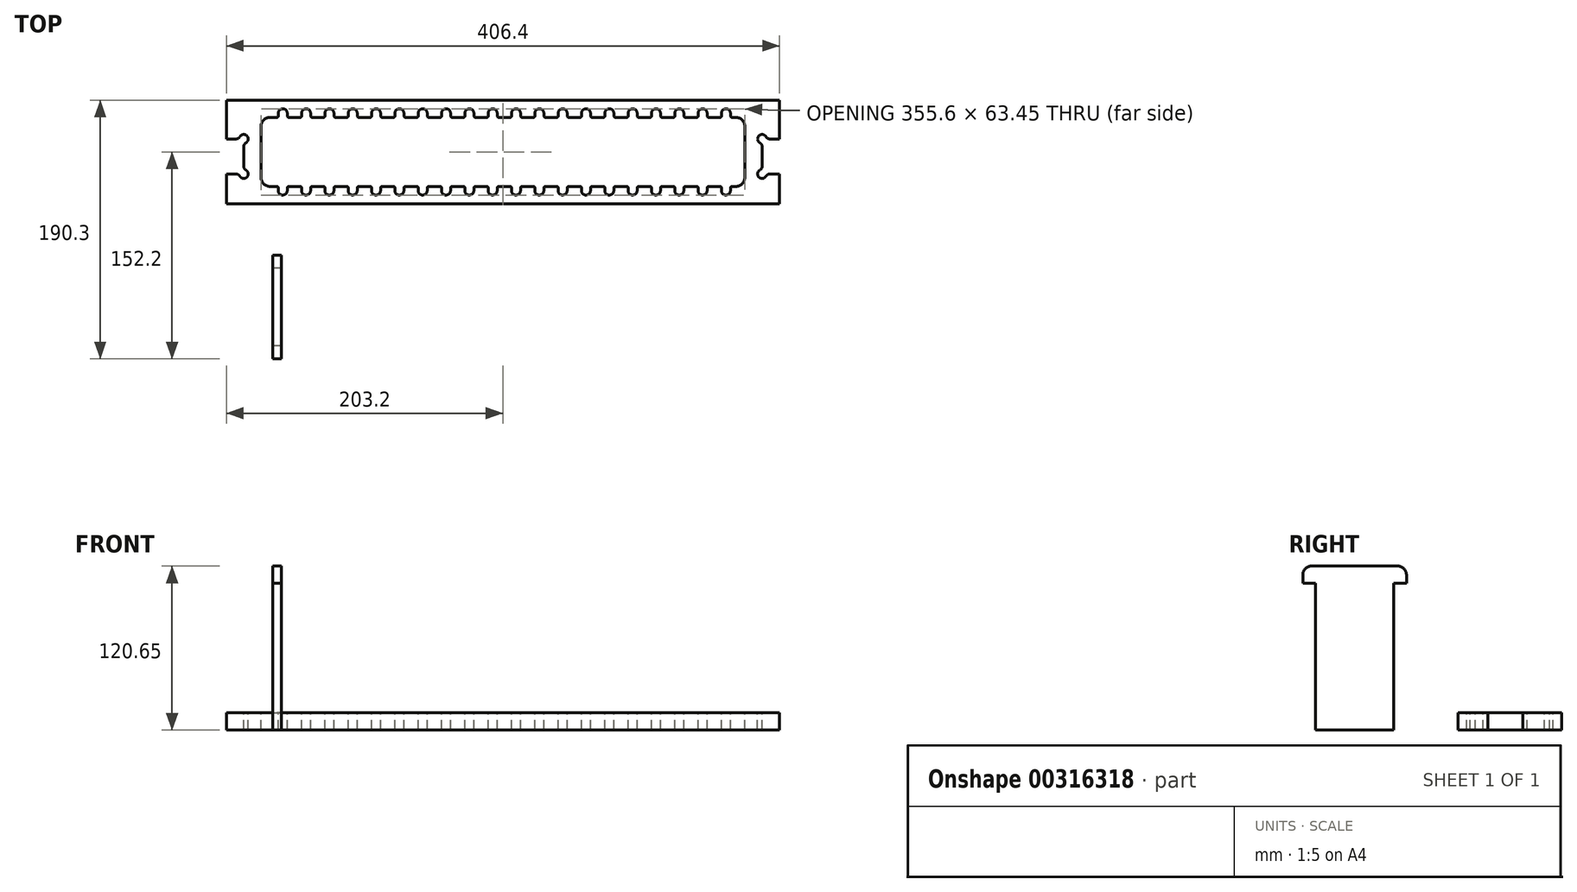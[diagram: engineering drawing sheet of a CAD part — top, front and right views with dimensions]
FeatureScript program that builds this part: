
annotation { "Feature Type Name" : "Feature", "Feature Type Description" : "" }
export const myFeature = defineFeature(function(context is Context, id is Id, definition is map)
    precondition{}
    {
        {
            var Q0;
            Q0=qCreatedBy(makeId("Top.planeOp"),FACE);
            var sketch = newSketch(context, id + "F0", { "sketchPlane" : qUnion([Q0])});
            skLineSegment(sketch, "E0.bottom", {"start": v(0, 0) * mm, "end": v(406.4, 0) * mm});
            skLineSegment(sketch, "E0.top", {"start": v(0, 76.2) * mm, "end": v(406.4, 76.2) * mm});
            skLineSegment(sketch, "E0.left", {"start": v(0, 0) * mm, "end": v(0, 76.2) * mm});
            skLineSegment(sketch, "E0.right", {"start": v(406.4, 0) * mm, "end": v(406.4, 76.2) * mm});
            skSolve(sketch);
        }
        {
            var Q0;
            Q0=qSketchRegion(id+"F0",true);
            extrude(context, id + "F1", {"entities" : qUnion([Q0]), "depth" : 12.7 * mm});
        }
        {
            var Q0;
            Q0=makeQuery(id+"F1.opExtrude","CAP_FACE",FACE,{"disambiguationData":[OSD([sQuery(id+"F0.wireOp",EDGE,"E0.bottom"),sQuery(id+"F0.wireOp",EDGE,"E0.top"),sQuery(id+"F0.wireOp",EDGE,"E0.left"),sQuery(id+"F0.wireOp",EDGE,"E0.right")])],"isStart":false});
            var sketch = newSketch(context, id + "F2", { "sketchPlane" : qUnion([Q0])});
            skLineSegment(sketch, "E1", {"start": v(0, 38.1) * mm, "end": v(103.18, 38.1) * mm, "construction": true});
            skLineSegment(sketch, "E2", {"start": v(203.2, 76.2) * mm, "end": v(203.2, 0) * mm, "construction": true});
            skLineSegment(sketch, "E3.bottom", {"start": v(0, 47.63) * mm, "end": v(7.05, 47.63) * mm});
            skLineSegment(sketch, "E3.top", {"start": v(0, 21.84) * mm, "end": v(7.05, 21.84) * mm});
            skLineSegment(sketch, "E3.left", {"start": v(0, 47.63) * mm, "end": v(0, 21.84) * mm});
            skLineSegment(sketch, "E3.right", {"start": v(12.7, 41.98) * mm, "end": v(12.7, 27.49) * mm});
            skArc(sketch, "E4", {"start": v(14.32, 44.75) * mm, "mid": v(15.03, 49.96) * mm, "end": v(9.82, 49.24) * mm});
            skArc(sketch, "E5", {"start": v(9.82, 20.23) * mm, "mid": v(15.03, 19.5) * mm, "end": v(14.32, 24.72) * mm});
            skPoint(sketch, "E6.visualSharp", {"position": v(9.4, 47.63) * mm});
            skArc(sketch, "E6.filletArc", {"start": v(7.05, 47.63) * mm, "mid": v(8.66, 48.06) * mm, "end": v(9.82, 49.24) * mm});
            skPoint(sketch, "E7.visualSharp", {"position": v(9.4, 21.84) * mm});
            skArc(sketch, "E7.filletArc", {"start": v(9.82, 20.23) * mm, "mid": v(8.66, 21.4) * mm, "end": v(7.05, 21.84) * mm});
            skPoint(sketch, "E8.visualSharp", {"position": v(12.7, 44.32) * mm});
            skArc(sketch, "E8.filletArc", {"start": v(14.32, 44.75) * mm, "mid": v(13.13, 43.58) * mm, "end": v(12.7, 41.98) * mm});
            skPoint(sketch, "E9.visualSharp", {"position": v(12.7, 25.15) * mm});
            skArc(sketch, "E9.filletArc", {"start": v(12.7, 27.49) * mm, "mid": v(13.13, 25.89) * mm, "end": v(14.32, 24.72) * mm});
            skArc(sketch, "E10.MirrorCS", {"start": v(393.7, 27.49) * mm, "mid": v(393.27, 25.89) * mm, "end": v(392.08, 24.72) * mm});
            skArc(sketch, "E11.MirrorCS", {"start": v(399.35, 47.63) * mm, "mid": v(397.74, 48.06) * mm, "end": v(396.58, 49.24) * mm});
            skArc(sketch, "E12.MirrorCS", {"start": v(392.08, 44.75) * mm, "mid": v(391.37, 49.96) * mm, "end": v(396.58, 49.24) * mm});
            skLineSegment(sketch, "E13.MirrorCS", {"start": v(406.4, 47.63) * mm, "end": v(399.35, 47.63) * mm});
            skArc(sketch, "E14.MirrorCS", {"start": v(396.58, 20.23) * mm, "mid": v(397.74, 21.4) * mm, "end": v(399.35, 21.84) * mm});
            skArc(sketch, "E15.MirrorCS", {"start": v(392.08, 44.75) * mm, "mid": v(393.27, 43.58) * mm, "end": v(393.7, 41.98) * mm});
            skLineSegment(sketch, "E16.MirrorCS", {"start": v(406.4, 21.84) * mm, "end": v(399.35, 21.84) * mm});
            skPoint(sketch, "E17.MirrorP", {"position": v(397, 47.63) * mm});
            skPoint(sketch, "E18.MirrorP", {"position": v(393.7, 25.15) * mm});
            skArc(sketch, "E19.MirrorCS", {"start": v(396.58, 20.23) * mm, "mid": v(391.37, 19.5) * mm, "end": v(392.08, 24.72) * mm});
            skPoint(sketch, "E20.MirrorP", {"position": v(393.7, 44.32) * mm});
            skPoint(sketch, "E21.MirrorP", {"position": v(397, 21.84) * mm});
            skLineSegment(sketch, "E22.MirrorCS", {"start": v(393.7, 41.98) * mm, "end": v(393.7, 27.49) * mm});
            skLineSegment(sketch, "E23.MirrorCS", {"start": v(406.4, 47.63) * mm, "end": v(406.4, 21.84) * mm});
            skSolve(sketch);
        }
        {
            var Q0;
            Q0=qSketchRegion(id+"F2",true);
            extrude(context, id + "F3", {"entities" : qUnion([Q0]), "operationType" : NewBodyOperationType.REMOVE, "oppositeDirection" : true, "depth" : 25.4 * mm});
        }
        {
            var Q0;
            Q0=makeQuery(id+"F1.opExtrude","CAP_FACE",FACE,{"disambiguationData":[OSD([sQuery(id+"F0.wireOp",EDGE,"E0.bottom"),sQuery(id+"F0.wireOp",EDGE,"E0.top"),sQuery(id+"F0.wireOp",EDGE,"E0.left"),sQuery(id+"F0.wireOp",EDGE,"E0.right")])],"isStart":false});
            var sketch = newSketch(context, id + "F4", { "sketchPlane" : qUnion([Q0])});
            skLineSegment(sketch, "E24.bottom", {"start": v(25.4, 12.7) * mm, "end": v(381, 12.7) * mm});
            skLineSegment(sketch, "E24.top", {"start": v(25.4, 63.5) * mm, "end": v(381, 63.5) * mm});
            skLineSegment(sketch, "E24.left", {"start": v(25.4, 12.7) * mm, "end": v(25.4, 63.5) * mm});
            skLineSegment(sketch, "E24.right", {"start": v(381, 12.7) * mm, "end": v(381, 63.5) * mm});
            skSolve(sketch);
        }
        {
            var Q0;
            Q0 = qSketchRegion(id + "F4", true);
            extrude(context, id + "F5", {"entities" : qUnion([Q0]), "operationType" : NewBodyOperationType.REMOVE, "oppositeDirection" : true, "depth" : 25.4 * mm});
        }
        {
            var Q0;
            Q0=makeQuery(id+"F5.boolean.opBoolean","COPY",EDGE,{"derivedFrom":makeQuery(id+"F5.opExtrude","SWEPT_EDGE",EDGE,{"disambiguationData":[OSD([sQuery(id+"F4.wireOp",EDGE,"E24.top"),sQuery(id+"F4.wireOp",EDGE,"E24.left")])]})});
            var Q1;
            Q1=makeQuery(id+"F5.boolean.opBoolean","COPY",EDGE,{"derivedFrom":makeQuery(id+"F5.opExtrude","SWEPT_EDGE",EDGE,{"disambiguationData":[OSD([sQuery(id+"F4.wireOp",EDGE,"E24.top"),sQuery(id+"F4.wireOp",EDGE,"E24.right")])]})});
            var Q2;
            Q2=makeQuery(id+"F5.boolean.opBoolean","COPY",EDGE,{"derivedFrom":makeQuery(id+"F5.opExtrude","SWEPT_EDGE",EDGE,{"disambiguationData":[OSD([sQuery(id+"F4.wireOp",EDGE,"E24.bottom"),sQuery(id+"F4.wireOp",EDGE,"E24.right")])]})});
            var Q3;
            Q3=makeQuery(id+"F5.boolean.opBoolean","COPY",EDGE,{"derivedFrom":makeQuery(id+"F5.opExtrude","SWEPT_EDGE",EDGE,{"disambiguationData":[OSD([sQuery(id+"F4.wireOp",EDGE,"E24.bottom"),sQuery(id+"F4.wireOp",EDGE,"E24.left")])]})});
            fillet(context, id + "F6", {"entities" : qUnion([Q0, Q1, Q2, Q3]), "radius" : 6.6 * mm, "tangentPropagation" : true, "allowEdgeOverflow" : false});
        }
        {
            var Q0;
            Q0=makeQuery(id+"F1.opExtrude","CAP_FACE",FACE,{"disambiguationData":[OSD([sQuery(id+"F0.wireOp",EDGE,"E0.bottom"),sQuery(id+"F0.wireOp",EDGE,"E0.top"),sQuery(id+"F0.wireOp",EDGE,"E0.left"),sQuery(id+"F0.wireOp",EDGE,"E0.right")])],"isStart":false});
            var sketch = newSketch(context, id + "F7", { "sketchPlane" : qUnion([Q0])});
            skLineSegment(sketch, "E25", {"start": v(38.1, 11.68) * mm, "end": v(38.1, 8.9) * mm});
            skLineSegment(sketch, "E26", {"start": v(44.7, 9.7) * mm, "end": v(44.7, 11.68) * mm});
            skArc(sketch, "E27", {"start": v(38.1, 8.9) * mm, "mid": v(41.76, 6.38) * mm, "end": v(44.7, 9.7) * mm});
            skLineSegment(sketch, "E28", {"start": v(45.72, 12.7) * mm, "end": v(54.23, 12.7) * mm});
            skLineSegment(sketch, "E29", {"start": v(34.7, 28.65) * mm, "end": v(49.72, 28.65) * mm});
            skPoint(sketch, "E30.visualSharp", {"position": v(33.68, 28.65) * mm});
            skArc(sketch, "E30.filletArc", {"start": v(34.7, 28.65) * mm, "mid": v(33.98, 28.35) * mm, "end": v(33.68, 27.64) * mm});
            skPoint(sketch, "E31.visualSharp", {"position": v(38.1, 12.7) * mm});
            skArc(sketch, "E31.filletArc", {"start": v(38.1, 11.68) * mm, "mid": v(37.8, 12.4) * mm, "end": v(37.08, 12.7) * mm});
            skPoint(sketch, "E32.visualSharp", {"position": v(44.7, 12.7) * mm});
            skArc(sketch, "E32.filletArc", {"start": v(45.72, 12.7) * mm, "mid": v(45, 12.4) * mm, "end": v(44.7, 11.68) * mm});
            skLineSegment(sketch, "E33", {"start": v(25.4, 38.1) * mm, "end": v(381, 38.1) * mm, "construction": true});
            skLineSegment(sketch, "E34", {"start": v(37.08, 12.7) * mm, "end": v(37.08, 16.94) * mm});
            skLineSegment(sketch, "E35", {"start": v(37.08, 16.94) * mm, "end": v(54.23, 16.94) * mm});
            skLineSegment(sketch, "E36", {"start": v(54.23, 16.94) * mm, "end": v(54.23, 12.7) * mm});
            skLineSegment(sketch, "E37.1.0.0", {"start": v(55.25, 11.68) * mm, "end": v(55.25, 8.9) * mm});
            skLineSegment(sketch, "E37.1.0.1", {"start": v(61.85, 9.7) * mm, "end": v(61.85, 11.68) * mm});
            skArc(sketch, "E37.1.0.2", {"start": v(55.25, 8.9) * mm, "mid": v(58.9, 6.38) * mm, "end": v(61.85, 9.7) * mm});
            skLineSegment(sketch, "E37.1.0.3", {"start": v(62.87, 12.7) * mm, "end": v(71.37, 12.7) * mm});
            skArc(sketch, "E37.1.0.4", {"start": v(55.25, 11.68) * mm, "mid": v(54.95, 12.4) * mm, "end": v(54.23, 12.7) * mm});
            skArc(sketch, "E37.1.0.5", {"start": v(62.87, 12.7) * mm, "mid": v(62.15, 12.4) * mm, "end": v(61.85, 11.68) * mm});
            skLineSegment(sketch, "E37.1.0.6", {"start": v(54.23, 12.7) * mm, "end": v(54.23, 16.94) * mm});
            skLineSegment(sketch, "E37.1.0.7", {"start": v(54.23, 16.94) * mm, "end": v(71.37, 16.94) * mm});
            skLineSegment(sketch, "E37.1.0.8", {"start": v(71.37, 16.94) * mm, "end": v(71.37, 12.7) * mm});
            skPoint(sketch, "E37.1.0.9", {"position": v(61.85, 12.7) * mm});
            skPoint(sketch, "E37.1.0.10", {"position": v(55.25, 12.7) * mm});
            skLineSegment(sketch, "E37.2.0.0", {"start": v(72.4, 11.68) * mm, "end": v(72.4, 8.9) * mm});
            skLineSegment(sketch, "E37.2.0.1", {"start": v(79, 9.7) * mm, "end": v(79, 11.68) * mm});
            skArc(sketch, "E37.2.0.2", {"start": v(72.4, 8.9) * mm, "mid": v(76.05, 6.38) * mm, "end": v(79, 9.7) * mm});
            skLineSegment(sketch, "E37.2.0.3", {"start": v(80, 12.7) * mm, "end": v(88.52, 12.7) * mm});
            skArc(sketch, "E37.2.0.4", {"start": v(72.4, 11.68) * mm, "mid": v(72.1, 12.4) * mm, "end": v(71.37, 12.7) * mm});
            skArc(sketch, "E37.2.0.5", {"start": v(80, 12.7) * mm, "mid": v(79.3, 12.4) * mm, "end": v(79, 11.68) * mm});
            skLineSegment(sketch, "E37.2.0.6", {"start": v(71.37, 12.7) * mm, "end": v(71.37, 16.94) * mm});
            skLineSegment(sketch, "E37.2.0.7", {"start": v(71.37, 16.94) * mm, "end": v(88.52, 16.94) * mm});
            skLineSegment(sketch, "E37.2.0.8", {"start": v(88.52, 16.94) * mm, "end": v(88.52, 12.7) * mm});
            skPoint(sketch, "E37.2.0.9", {"position": v(79, 12.7) * mm});
            skPoint(sketch, "E37.2.0.10", {"position": v(72.4, 12.7) * mm});
            skLineSegment(sketch, "E37.3.0.0", {"start": v(89.53, 11.68) * mm, "end": v(89.53, 8.9) * mm});
            skLineSegment(sketch, "E37.3.0.1", {"start": v(96.14, 9.7) * mm, "end": v(96.14, 11.68) * mm});
            skArc(sketch, "E37.3.0.2", {"start": v(89.53, 8.9) * mm, "mid": v(93.2, 6.38) * mm, "end": v(96.14, 9.7) * mm});
            skLineSegment(sketch, "E37.3.0.3", {"start": v(97.15, 12.7) * mm, "end": v(105.66, 12.7) * mm});
            skArc(sketch, "E37.3.0.4", {"start": v(89.54, 11.68) * mm, "mid": v(89.24, 12.4) * mm, "end": v(88.52, 12.7) * mm});
            skArc(sketch, "E37.3.0.5", {"start": v(97.15, 12.7) * mm, "mid": v(96.44, 12.4) * mm, "end": v(96.14, 11.68) * mm});
            skLineSegment(sketch, "E37.3.0.6", {"start": v(88.52, 12.7) * mm, "end": v(88.52, 16.94) * mm});
            skLineSegment(sketch, "E37.3.0.7", {"start": v(88.52, 16.94) * mm, "end": v(105.66, 16.94) * mm});
            skLineSegment(sketch, "E37.3.0.8", {"start": v(105.66, 16.94) * mm, "end": v(105.66, 12.7) * mm});
            skPoint(sketch, "E37.3.0.9", {"position": v(96.14, 12.7) * mm});
            skPoint(sketch, "E37.3.0.10", {"position": v(89.53, 12.7) * mm});
            skLineSegment(sketch, "E37.4.0.0", {"start": v(106.68, 11.68) * mm, "end": v(106.68, 8.9) * mm});
            skLineSegment(sketch, "E37.4.0.1", {"start": v(113.28, 9.7) * mm, "end": v(113.28, 11.68) * mm});
            skArc(sketch, "E37.4.0.2", {"start": v(106.68, 8.9) * mm, "mid": v(110.34, 6.38) * mm, "end": v(113.28, 9.7) * mm});
            skLineSegment(sketch, "E37.4.0.3", {"start": v(114.3, 12.7) * mm, "end": v(122.8, 12.7) * mm});
            skArc(sketch, "E37.4.0.4", {"start": v(106.68, 11.68) * mm, "mid": v(106.38, 12.4) * mm, "end": v(105.66, 12.7) * mm});
            skArc(sketch, "E37.4.0.5", {"start": v(114.3, 12.7) * mm, "mid": v(113.58, 12.4) * mm, "end": v(113.28, 11.68) * mm});
            skLineSegment(sketch, "E37.4.0.6", {"start": v(105.66, 12.7) * mm, "end": v(105.66, 16.94) * mm});
            skLineSegment(sketch, "E37.4.0.7", {"start": v(105.66, 16.94) * mm, "end": v(122.8, 16.94) * mm});
            skLineSegment(sketch, "E37.4.0.8", {"start": v(122.8, 16.94) * mm, "end": v(122.8, 12.7) * mm});
            skPoint(sketch, "E37.4.0.9", {"position": v(113.28, 12.7) * mm});
            skPoint(sketch, "E37.4.0.10", {"position": v(106.68, 12.7) * mm});
            skLineSegment(sketch, "E37.5.0.0", {"start": v(123.82, 11.68) * mm, "end": v(123.82, 8.9) * mm});
            skLineSegment(sketch, "E37.5.0.1", {"start": v(130.43, 9.7) * mm, "end": v(130.43, 11.68) * mm});
            skArc(sketch, "E37.5.0.2", {"start": v(123.82, 8.9) * mm, "mid": v(127.49, 6.38) * mm, "end": v(130.43, 9.7) * mm});
            skLineSegment(sketch, "E37.5.0.3", {"start": v(131.44, 12.7) * mm, "end": v(139.95, 12.7) * mm});
            skArc(sketch, "E37.5.0.4", {"start": v(123.83, 11.68) * mm, "mid": v(123.53, 12.4) * mm, "end": v(122.8, 12.7) * mm});
            skArc(sketch, "E37.5.0.5", {"start": v(131.44, 12.7) * mm, "mid": v(130.73, 12.4) * mm, "end": v(130.43, 11.68) * mm});
            skLineSegment(sketch, "E37.5.0.6", {"start": v(122.8, 12.7) * mm, "end": v(122.8, 16.94) * mm});
            skLineSegment(sketch, "E37.5.0.7", {"start": v(122.8, 16.94) * mm, "end": v(139.95, 16.94) * mm});
            skLineSegment(sketch, "E37.5.0.8", {"start": v(139.95, 16.94) * mm, "end": v(139.95, 12.7) * mm});
            skPoint(sketch, "E37.5.0.9", {"position": v(130.43, 12.7) * mm});
            skPoint(sketch, "E37.5.0.10", {"position": v(123.82, 12.7) * mm});
            skLineSegment(sketch, "E37.6.0.0", {"start": v(140.97, 11.68) * mm, "end": v(140.97, 8.9) * mm});
            skLineSegment(sketch, "E37.6.0.1", {"start": v(147.57, 9.7) * mm, "end": v(147.57, 11.68) * mm});
            skArc(sketch, "E37.6.0.2", {"start": v(140.97, 8.9) * mm, "mid": v(144.63, 6.38) * mm, "end": v(147.57, 9.7) * mm});
            skLineSegment(sketch, "E37.6.0.3", {"start": v(148.6, 12.7) * mm, "end": v(157.1, 12.7) * mm});
            skArc(sketch, "E37.6.0.4", {"start": v(140.97, 11.68) * mm, "mid": v(140.67, 12.4) * mm, "end": v(139.95, 12.7) * mm});
            skArc(sketch, "E37.6.0.5", {"start": v(148.6, 12.7) * mm, "mid": v(147.87, 12.4) * mm, "end": v(147.57, 11.68) * mm});
            skLineSegment(sketch, "E37.6.0.6", {"start": v(139.95, 12.7) * mm, "end": v(139.95, 16.94) * mm});
            skLineSegment(sketch, "E37.6.0.7", {"start": v(139.95, 16.94) * mm, "end": v(157.1, 16.94) * mm});
            skLineSegment(sketch, "E37.6.0.8", {"start": v(157.1, 16.94) * mm, "end": v(157.1, 12.7) * mm});
            skPoint(sketch, "E37.6.0.9", {"position": v(147.57, 12.7) * mm});
            skPoint(sketch, "E37.6.0.10", {"position": v(140.97, 12.7) * mm});
            skLineSegment(sketch, "E37.7.0.0", {"start": v(158.12, 11.68) * mm, "end": v(158.12, 8.9) * mm});
            skLineSegment(sketch, "E37.7.0.1", {"start": v(164.72, 9.7) * mm, "end": v(164.72, 11.68) * mm});
            skArc(sketch, "E37.7.0.2", {"start": v(158.12, 8.9) * mm, "mid": v(161.78, 6.38) * mm, "end": v(164.72, 9.7) * mm});
            skLineSegment(sketch, "E37.7.0.3", {"start": v(165.74, 12.7) * mm, "end": v(174.24, 12.7) * mm});
            skArc(sketch, "E37.7.0.4", {"start": v(158.12, 11.68) * mm, "mid": v(157.82, 12.4) * mm, "end": v(157.1, 12.7) * mm});
            skArc(sketch, "E37.7.0.5", {"start": v(165.74, 12.7) * mm, "mid": v(165.02, 12.4) * mm, "end": v(164.72, 11.68) * mm});
            skLineSegment(sketch, "E37.7.0.6", {"start": v(157.1, 12.7) * mm, "end": v(157.1, 16.94) * mm});
            skLineSegment(sketch, "E37.7.0.7", {"start": v(157.1, 16.94) * mm, "end": v(174.24, 16.94) * mm});
            skLineSegment(sketch, "E37.7.0.8", {"start": v(174.24, 16.94) * mm, "end": v(174.24, 12.7) * mm});
            skPoint(sketch, "E37.7.0.9", {"position": v(164.72, 12.7) * mm});
            skPoint(sketch, "E37.7.0.10", {"position": v(158.12, 12.7) * mm});
            skLineSegment(sketch, "E37.8.0.0", {"start": v(175.26, 11.68) * mm, "end": v(175.26, 8.9) * mm});
            skLineSegment(sketch, "E37.8.0.1", {"start": v(181.86, 9.7) * mm, "end": v(181.86, 11.68) * mm});
            skArc(sketch, "E37.8.0.2", {"start": v(175.26, 8.9) * mm, "mid": v(178.92, 6.38) * mm, "end": v(181.86, 9.7) * mm});
            skLineSegment(sketch, "E37.8.0.3", {"start": v(182.88, 12.7) * mm, "end": v(191.39, 12.7) * mm});
            skArc(sketch, "E37.8.0.4", {"start": v(175.26, 11.68) * mm, "mid": v(174.96, 12.4) * mm, "end": v(174.24, 12.7) * mm});
            skArc(sketch, "E37.8.0.5", {"start": v(182.88, 12.7) * mm, "mid": v(182.16, 12.4) * mm, "end": v(181.86, 11.68) * mm});
            skLineSegment(sketch, "E37.8.0.6", {"start": v(174.24, 12.7) * mm, "end": v(174.24, 16.94) * mm});
            skLineSegment(sketch, "E37.8.0.7", {"start": v(174.24, 16.94) * mm, "end": v(191.39, 16.94) * mm});
            skLineSegment(sketch, "E37.8.0.8", {"start": v(191.39, 16.94) * mm, "end": v(191.39, 12.7) * mm});
            skPoint(sketch, "E37.8.0.9", {"position": v(181.86, 12.7) * mm});
            skPoint(sketch, "E37.8.0.10", {"position": v(175.26, 12.7) * mm});
            skLineSegment(sketch, "E37.9.0.0", {"start": v(192.4, 11.68) * mm, "end": v(192.4, 8.9) * mm});
            skLineSegment(sketch, "E37.9.0.1", {"start": v(199, 9.7) * mm, "end": v(199, 11.68) * mm});
            skArc(sketch, "E37.9.0.2", {"start": v(192.4, 8.9) * mm, "mid": v(196.07, 6.38) * mm, "end": v(199, 9.7) * mm});
            skLineSegment(sketch, "E37.9.0.3", {"start": v(200.03, 12.7) * mm, "end": v(208.53, 12.7) * mm});
            skArc(sketch, "E37.9.0.4", {"start": v(192.4, 11.68) * mm, "mid": v(192.1, 12.4) * mm, "end": v(191.39, 12.7) * mm});
            skArc(sketch, "E37.9.0.5", {"start": v(200.03, 12.7) * mm, "mid": v(199.3, 12.4) * mm, "end": v(199, 11.68) * mm});
            skLineSegment(sketch, "E37.9.0.6", {"start": v(191.39, 12.7) * mm, "end": v(191.39, 16.94) * mm});
            skLineSegment(sketch, "E37.9.0.7", {"start": v(191.39, 16.94) * mm, "end": v(208.53, 16.94) * mm});
            skLineSegment(sketch, "E37.9.0.8", {"start": v(208.53, 16.94) * mm, "end": v(208.53, 12.7) * mm});
            skPoint(sketch, "E37.9.0.9", {"position": v(199, 12.7) * mm});
            skPoint(sketch, "E37.9.0.10", {"position": v(192.4, 12.7) * mm});
            skLineSegment(sketch, "E37.10.0.0", {"start": v(209.55, 11.68) * mm, "end": v(209.55, 8.9) * mm});
            skLineSegment(sketch, "E37.10.0.1", {"start": v(216.15, 9.7) * mm, "end": v(216.15, 11.68) * mm});
            skArc(sketch, "E37.10.0.2", {"start": v(209.55, 8.9) * mm, "mid": v(213.21, 6.38) * mm, "end": v(216.15, 9.7) * mm});
            skLineSegment(sketch, "E37.10.0.3", {"start": v(217.17, 12.7) * mm, "end": v(225.68, 12.7) * mm});
            skArc(sketch, "E37.10.0.4", {"start": v(209.55, 11.68) * mm, "mid": v(209.25, 12.4) * mm, "end": v(208.53, 12.7) * mm});
            skArc(sketch, "E37.10.0.5", {"start": v(217.17, 12.7) * mm, "mid": v(216.45, 12.4) * mm, "end": v(216.15, 11.68) * mm});
            skLineSegment(sketch, "E37.10.0.6", {"start": v(208.53, 12.7) * mm, "end": v(208.53, 16.94) * mm});
            skLineSegment(sketch, "E37.10.0.7", {"start": v(208.53, 16.94) * mm, "end": v(225.68, 16.94) * mm});
            skLineSegment(sketch, "E37.10.0.8", {"start": v(225.68, 16.94) * mm, "end": v(225.68, 12.7) * mm});
            skPoint(sketch, "E37.10.0.9", {"position": v(216.15, 12.7) * mm});
            skPoint(sketch, "E37.10.0.10", {"position": v(209.55, 12.7) * mm});
            skLineSegment(sketch, "E37.11.0.0", {"start": v(226.7, 11.68) * mm, "end": v(226.7, 8.9) * mm});
            skLineSegment(sketch, "E37.11.0.1", {"start": v(233.3, 9.7) * mm, "end": v(233.3, 11.68) * mm});
            skArc(sketch, "E37.11.0.2", {"start": v(226.7, 8.9) * mm, "mid": v(230.36, 6.38) * mm, "end": v(233.3, 9.7) * mm});
            skLineSegment(sketch, "E37.11.0.3", {"start": v(234.31, 12.7) * mm, "end": v(242.82, 12.7) * mm});
            skArc(sketch, "E37.11.0.4", {"start": v(226.7, 11.68) * mm, "mid": v(226.4, 12.4) * mm, "end": v(225.68, 12.7) * mm});
            skArc(sketch, "E37.11.0.5", {"start": v(234.31, 12.7) * mm, "mid": v(233.6, 12.4) * mm, "end": v(233.3, 11.68) * mm});
            skLineSegment(sketch, "E37.11.0.6", {"start": v(225.68, 12.7) * mm, "end": v(225.68, 16.94) * mm});
            skLineSegment(sketch, "E37.11.0.7", {"start": v(225.68, 16.94) * mm, "end": v(242.82, 16.94) * mm});
            skLineSegment(sketch, "E37.11.0.8", {"start": v(242.82, 16.94) * mm, "end": v(242.82, 12.7) * mm});
            skPoint(sketch, "E37.11.0.9", {"position": v(233.3, 12.7) * mm});
            skPoint(sketch, "E37.11.0.10", {"position": v(226.7, 12.7) * mm});
            skLineSegment(sketch, "E37.12.0.0", {"start": v(243.84, 11.68) * mm, "end": v(243.84, 8.9) * mm});
            skLineSegment(sketch, "E37.12.0.1", {"start": v(250.44, 9.7) * mm, "end": v(250.44, 11.68) * mm});
            skArc(sketch, "E37.12.0.2", {"start": v(243.84, 8.9) * mm, "mid": v(247.5, 6.38) * mm, "end": v(250.44, 9.7) * mm});
            skLineSegment(sketch, "E37.12.0.3", {"start": v(251.46, 12.7) * mm, "end": v(259.97, 12.7) * mm});
            skArc(sketch, "E37.12.0.4", {"start": v(243.84, 11.68) * mm, "mid": v(243.54, 12.4) * mm, "end": v(242.82, 12.7) * mm});
            skArc(sketch, "E37.12.0.5", {"start": v(251.46, 12.7) * mm, "mid": v(250.74, 12.4) * mm, "end": v(250.44, 11.68) * mm});
            skLineSegment(sketch, "E37.12.0.6", {"start": v(242.82, 12.7) * mm, "end": v(242.82, 16.94) * mm});
            skLineSegment(sketch, "E37.12.0.7", {"start": v(242.82, 16.94) * mm, "end": v(259.97, 16.94) * mm});
            skLineSegment(sketch, "E37.12.0.8", {"start": v(259.97, 16.94) * mm, "end": v(259.97, 12.7) * mm});
            skPoint(sketch, "E37.12.0.9", {"position": v(250.44, 12.7) * mm});
            skPoint(sketch, "E37.12.0.10", {"position": v(243.84, 12.7) * mm});
            skLineSegment(sketch, "E37.13.0.0", {"start": v(260.99, 11.68) * mm, "end": v(260.99, 8.9) * mm});
            skLineSegment(sketch, "E37.13.0.1", {"start": v(267.59, 9.7) * mm, "end": v(267.59, 11.68) * mm});
            skArc(sketch, "E37.13.0.2", {"start": v(260.99, 8.89) * mm, "mid": v(264.65, 6.38) * mm, "end": v(267.59, 9.7) * mm});
            skLineSegment(sketch, "E37.13.0.3", {"start": v(268.6, 12.7) * mm, "end": v(277.11, 12.7) * mm});
            skArc(sketch, "E37.13.0.4", {"start": v(260.99, 11.68) * mm, "mid": v(260.69, 12.4) * mm, "end": v(259.97, 12.7) * mm});
            skArc(sketch, "E37.13.0.5", {"start": v(268.6, 12.7) * mm, "mid": v(267.89, 12.4) * mm, "end": v(267.59, 11.68) * mm});
            skLineSegment(sketch, "E37.13.0.6", {"start": v(259.97, 12.7) * mm, "end": v(259.97, 16.94) * mm});
            skLineSegment(sketch, "E37.13.0.7", {"start": v(259.97, 16.94) * mm, "end": v(277.11, 16.94) * mm});
            skLineSegment(sketch, "E37.13.0.8", {"start": v(277.11, 16.94) * mm, "end": v(277.11, 12.7) * mm});
            skPoint(sketch, "E37.13.0.9", {"position": v(267.59, 12.7) * mm});
            skPoint(sketch, "E37.13.0.10", {"position": v(260.99, 12.7) * mm});
            skLineSegment(sketch, "E37.14.0.0", {"start": v(278.13, 11.68) * mm, "end": v(278.13, 8.9) * mm});
            skLineSegment(sketch, "E37.14.0.1", {"start": v(284.73, 9.7) * mm, "end": v(284.73, 11.68) * mm});
            skArc(sketch, "E37.14.0.2", {"start": v(278.13, 8.9) * mm, "mid": v(281.8, 6.38) * mm, "end": v(284.73, 9.7) * mm});
            skLineSegment(sketch, "E37.14.0.3", {"start": v(285.75, 12.7) * mm, "end": v(294.26, 12.7) * mm});
            skArc(sketch, "E37.14.0.4", {"start": v(278.13, 11.68) * mm, "mid": v(277.83, 12.4) * mm, "end": v(277.11, 12.7) * mm});
            skArc(sketch, "E37.14.0.5", {"start": v(285.75, 12.7) * mm, "mid": v(285.03, 12.4) * mm, "end": v(284.73, 11.68) * mm});
            skLineSegment(sketch, "E37.14.0.6", {"start": v(277.11, 12.7) * mm, "end": v(277.11, 16.94) * mm});
            skLineSegment(sketch, "E37.14.0.7", {"start": v(277.11, 16.94) * mm, "end": v(294.26, 16.94) * mm});
            skLineSegment(sketch, "E37.14.0.8", {"start": v(294.26, 16.94) * mm, "end": v(294.26, 12.7) * mm});
            skPoint(sketch, "E37.14.0.9", {"position": v(284.73, 12.7) * mm});
            skPoint(sketch, "E37.14.0.10", {"position": v(278.13, 12.7) * mm});
            skLineSegment(sketch, "E37.15.0.0", {"start": v(295.28, 11.68) * mm, "end": v(295.28, 8.9) * mm});
            skLineSegment(sketch, "E37.15.0.1", {"start": v(301.88, 9.7) * mm, "end": v(301.88, 11.68) * mm});
            skArc(sketch, "E37.15.0.2", {"start": v(295.27, 8.9) * mm, "mid": v(298.94, 6.38) * mm, "end": v(301.88, 9.7) * mm});
            skLineSegment(sketch, "E37.15.0.3", {"start": v(302.9, 12.7) * mm, "end": v(311.4, 12.7) * mm});
            skArc(sketch, "E37.15.0.4", {"start": v(295.28, 11.68) * mm, "mid": v(294.98, 12.4) * mm, "end": v(294.26, 12.7) * mm});
            skArc(sketch, "E37.15.0.5", {"start": v(302.9, 12.7) * mm, "mid": v(302.18, 12.4) * mm, "end": v(301.88, 11.68) * mm});
            skLineSegment(sketch, "E37.15.0.6", {"start": v(294.26, 12.7) * mm, "end": v(294.26, 16.94) * mm});
            skLineSegment(sketch, "E37.15.0.7", {"start": v(294.26, 16.94) * mm, "end": v(311.4, 16.94) * mm});
            skLineSegment(sketch, "E37.15.0.8", {"start": v(311.4, 16.94) * mm, "end": v(311.4, 12.7) * mm});
            skPoint(sketch, "E37.15.0.9", {"position": v(301.88, 12.7) * mm});
            skPoint(sketch, "E37.15.0.10", {"position": v(295.28, 12.7) * mm});
            skLineSegment(sketch, "E37.16.0.0", {"start": v(312.42, 11.68) * mm, "end": v(312.42, 8.9) * mm});
            skLineSegment(sketch, "E37.16.0.1", {"start": v(319.02, 9.7) * mm, "end": v(319.02, 11.68) * mm});
            skArc(sketch, "E37.16.0.2", {"start": v(312.42, 8.89) * mm, "mid": v(316.08, 6.38) * mm, "end": v(319.02, 9.7) * mm});
            skLineSegment(sketch, "E37.16.0.3", {"start": v(320.04, 12.7) * mm, "end": v(328.55, 12.7) * mm});
            skArc(sketch, "E37.16.0.4", {"start": v(312.42, 11.68) * mm, "mid": v(312.12, 12.4) * mm, "end": v(311.4, 12.7) * mm});
            skArc(sketch, "E37.16.0.5", {"start": v(320.04, 12.7) * mm, "mid": v(319.32, 12.4) * mm, "end": v(319.02, 11.68) * mm});
            skLineSegment(sketch, "E37.16.0.6", {"start": v(311.4, 12.7) * mm, "end": v(311.4, 16.94) * mm});
            skLineSegment(sketch, "E37.16.0.7", {"start": v(311.4, 16.94) * mm, "end": v(328.55, 16.94) * mm});
            skLineSegment(sketch, "E37.16.0.8", {"start": v(328.55, 16.94) * mm, "end": v(328.55, 12.7) * mm});
            skPoint(sketch, "E37.16.0.9", {"position": v(319.02, 12.7) * mm});
            skPoint(sketch, "E37.16.0.10", {"position": v(312.42, 12.7) * mm});
            skLineSegment(sketch, "E37.17.0.0", {"start": v(329.57, 11.68) * mm, "end": v(329.57, 8.9) * mm});
            skLineSegment(sketch, "E37.17.0.1", {"start": v(336.17, 9.7) * mm, "end": v(336.17, 11.68) * mm});
            skArc(sketch, "E37.17.0.2", {"start": v(329.56, 8.9) * mm, "mid": v(333.23, 6.38) * mm, "end": v(336.17, 9.7) * mm});
            skLineSegment(sketch, "E37.17.0.3", {"start": v(337.19, 12.7) * mm, "end": v(345.7, 12.7) * mm});
            skArc(sketch, "E37.17.0.4", {"start": v(329.57, 11.68) * mm, "mid": v(329.27, 12.4) * mm, "end": v(328.55, 12.7) * mm});
            skArc(sketch, "E37.17.0.5", {"start": v(337.19, 12.7) * mm, "mid": v(336.47, 12.4) * mm, "end": v(336.17, 11.68) * mm});
            skLineSegment(sketch, "E37.17.0.6", {"start": v(328.55, 12.7) * mm, "end": v(328.55, 16.94) * mm});
            skLineSegment(sketch, "E37.17.0.7", {"start": v(328.55, 16.94) * mm, "end": v(345.7, 16.94) * mm});
            skLineSegment(sketch, "E37.17.0.8", {"start": v(345.7, 16.94) * mm, "end": v(345.7, 12.7) * mm});
            skPoint(sketch, "E37.17.0.9", {"position": v(336.17, 12.7) * mm});
            skPoint(sketch, "E37.17.0.10", {"position": v(329.57, 12.7) * mm});
            skLineSegment(sketch, "E37.18.0.0", {"start": v(346.71, 11.68) * mm, "end": v(346.71, 8.9) * mm});
            skLineSegment(sketch, "E37.18.0.1", {"start": v(353.31, 9.7) * mm, "end": v(353.31, 11.68) * mm});
            skArc(sketch, "E37.18.0.2", {"start": v(346.7, 8.9) * mm, "mid": v(350.37, 6.38) * mm, "end": v(353.31, 9.7) * mm});
            skLineSegment(sketch, "E37.18.0.3", {"start": v(354.33, 12.7) * mm, "end": v(362.84, 12.7) * mm});
            skArc(sketch, "E37.18.0.4", {"start": v(346.71, 11.68) * mm, "mid": v(346.41, 12.4) * mm, "end": v(345.7, 12.7) * mm});
            skArc(sketch, "E37.18.0.5", {"start": v(354.33, 12.7) * mm, "mid": v(353.61, 12.4) * mm, "end": v(353.31, 11.68) * mm});
            skLineSegment(sketch, "E37.18.0.6", {"start": v(345.7, 12.7) * mm, "end": v(345.7, 16.94) * mm});
            skLineSegment(sketch, "E37.18.0.7", {"start": v(345.7, 16.94) * mm, "end": v(362.84, 16.94) * mm});
            skLineSegment(sketch, "E37.18.0.8", {"start": v(362.84, 16.94) * mm, "end": v(362.84, 12.7) * mm});
            skPoint(sketch, "E37.18.0.9", {"position": v(353.31, 12.7) * mm});
            skPoint(sketch, "E37.18.0.10", {"position": v(346.71, 12.7) * mm});
            skLineSegment(sketch, "E37.19.0.0", {"start": v(363.86, 11.68) * mm, "end": v(363.86, 8.9) * mm});
            skLineSegment(sketch, "E37.19.0.1", {"start": v(370.46, 9.7) * mm, "end": v(370.46, 11.68) * mm});
            skArc(sketch, "E37.19.0.2", {"start": v(363.86, 8.89) * mm, "mid": v(367.52, 6.38) * mm, "end": v(370.46, 9.7) * mm});
            skLineSegment(sketch, "E37.19.0.3", {"start": v(371.48, 12.7) * mm, "end": v(374.4, 12.7) * mm});
            skArc(sketch, "E37.19.0.4", {"start": v(363.86, 11.68) * mm, "mid": v(363.56, 12.4) * mm, "end": v(362.84, 12.7) * mm});
            skArc(sketch, "E37.19.0.5", {"start": v(371.48, 12.7) * mm, "mid": v(370.76, 12.4) * mm, "end": v(370.46, 11.68) * mm});
            skLineSegment(sketch, "E37.19.0.6", {"start": v(362.84, 12.7) * mm, "end": v(362.84, 16.94) * mm});
            skLineSegment(sketch, "E37.19.0.7", {"start": v(362.84, 16.94) * mm, "end": v(374.4, 16.94) * mm});
            skPoint(sketch, "E37.19.0.9", {"position": v(370.46, 12.7) * mm});
            skPoint(sketch, "E37.19.0.10", {"position": v(363.86, 12.7) * mm});
            skLineSegment(sketch, "E37.direction1", {"start": v(38.1, 8.9) * mm, "end": v(55.25, 8.9) * mm, "construction": true});
            skLineSegment(sketch, "E38.MirrorCS", {"start": v(294.26, 59.26) * mm, "end": v(294.26, 63.5) * mm});
            skLineSegment(sketch, "E39.MirrorCS", {"start": v(139.95, 59.26) * mm, "end": v(139.95, 63.5) * mm});
            skLineSegment(sketch, "E40.MirrorCS", {"start": v(259.97, 59.26) * mm, "end": v(259.97, 63.5) * mm});
            skLineSegment(sketch, "E41.MirrorCS", {"start": v(277.11, 63.5) * mm, "end": v(277.11, 59.26) * mm});
            skLineSegment(sketch, "E42.MirrorCS", {"start": v(105.66, 59.26) * mm, "end": v(105.66, 63.5) * mm});
            skLineSegment(sketch, "E43.MirrorCS", {"start": v(122.8, 63.5) * mm, "end": v(122.8, 59.26) * mm});
            skLineSegment(sketch, "E44.MirrorCS", {"start": v(225.68, 59.26) * mm, "end": v(225.68, 63.5) * mm});
            skLineSegment(sketch, "E45.MirrorCS", {"start": v(242.82, 63.5) * mm, "end": v(242.82, 59.26) * mm});
            skLineSegment(sketch, "E46.MirrorCS", {"start": v(362.84, 63.5) * mm, "end": v(362.84, 59.26) * mm});
            skLineSegment(sketch, "E47.MirrorCS", {"start": v(345.7, 59.26) * mm, "end": v(345.7, 63.5) * mm});
            skLineSegment(sketch, "E48.MirrorCS", {"start": v(54.23, 59.26) * mm, "end": v(54.23, 63.5) * mm});
            skLineSegment(sketch, "E49.MirrorCS", {"start": v(88.52, 63.5) * mm, "end": v(88.52, 59.26) * mm});
            skLineSegment(sketch, "E50.MirrorCS", {"start": v(71.37, 59.26) * mm, "end": v(71.37, 63.5) * mm});
            skLineSegment(sketch, "E51.MirrorCS", {"start": v(157.1, 59.26) * mm, "end": v(157.1, 63.5) * mm});
            skLineSegment(sketch, "E52.MirrorCS", {"start": v(174.24, 63.5) * mm, "end": v(174.24, 59.26) * mm});
            skLineSegment(sketch, "E53.MirrorCS", {"start": v(328.55, 63.5) * mm, "end": v(328.55, 59.26) * mm});
            skLineSegment(sketch, "E54.MirrorCS", {"start": v(311.4, 59.26) * mm, "end": v(311.4, 63.5) * mm});
            skArc(sketch, "E55.MirrorCS", {"start": v(243.84, 64.52) * mm, "mid": v(243.54, 63.8) * mm, "end": v(242.82, 63.5) * mm});
            skLineSegment(sketch, "E56.MirrorCS", {"start": v(208.53, 63.5) * mm, "end": v(208.53, 59.26) * mm});
            skLineSegment(sketch, "E57.MirrorCS", {"start": v(191.39, 59.26) * mm, "end": v(191.39, 63.5) * mm});
            skLineSegment(sketch, "E58.MirrorCS", {"start": v(55.25, 64.52) * mm, "end": v(55.25, 67.31) * mm});
            skLineSegment(sketch, "E59.MirrorCS", {"start": v(362.84, 59.26) * mm, "end": v(362.84, 63.5) * mm});
            skLineSegment(sketch, "E60.MirrorCS", {"start": v(105.66, 63.5) * mm, "end": v(105.66, 59.26) * mm});
            skLineSegment(sketch, "E61.MirrorCS", {"start": v(88.52, 59.26) * mm, "end": v(88.52, 63.5) * mm});
            skArc(sketch, "E62.MirrorCS", {"start": v(106.68, 64.52) * mm, "mid": v(106.38, 63.8) * mm, "end": v(105.66, 63.5) * mm});
            skLineSegment(sketch, "E63.MirrorCS", {"start": v(71.37, 63.5) * mm, "end": v(71.37, 59.26) * mm});
            skLineSegment(sketch, "E64.MirrorCS", {"start": v(345.7, 63.5) * mm, "end": v(345.7, 59.26) * mm});
            skLineSegment(sketch, "E65.MirrorCS", {"start": v(328.55, 59.26) * mm, "end": v(328.55, 63.5) * mm});
            skLineSegment(sketch, "E66.MirrorCS", {"start": v(174.24, 59.26) * mm, "end": v(174.24, 63.5) * mm});
            skLineSegment(sketch, "E67.MirrorCS", {"start": v(191.39, 63.5) * mm, "end": v(191.39, 59.26) * mm});
            skArc(sketch, "E68.MirrorCS", {"start": v(226.7, 64.52) * mm, "mid": v(226.4, 63.8) * mm, "end": v(225.68, 63.5) * mm});
            skLineSegment(sketch, "E69.MirrorCS", {"start": v(225.68, 63.5) * mm, "end": v(225.68, 59.26) * mm});
            skLineSegment(sketch, "E70.MirrorCS", {"start": v(208.53, 59.26) * mm, "end": v(208.53, 63.5) * mm});
            skLineSegment(sketch, "E71.MirrorCS", {"start": v(311.4, 63.5) * mm, "end": v(311.4, 59.26) * mm});
            skArc(sketch, "E72.MirrorCS", {"start": v(346.71, 64.52) * mm, "mid": v(346.41, 63.8) * mm, "end": v(345.7, 63.5) * mm});
            skArc(sketch, "E73.MirrorCS", {"start": v(260.99, 64.52) * mm, "mid": v(260.69, 63.8) * mm, "end": v(259.97, 63.5) * mm});
            skArc(sketch, "E74.MirrorCS", {"start": v(72.4, 64.52) * mm, "mid": v(72.1, 63.8) * mm, "end": v(71.37, 63.5) * mm});
            skArc(sketch, "E75.MirrorCS", {"start": v(140.97, 64.52) * mm, "mid": v(140.67, 63.8) * mm, "end": v(139.95, 63.5) * mm});
            skLineSegment(sketch, "E76.MirrorCS", {"start": v(259.97, 63.5) * mm, "end": v(259.97, 59.26) * mm});
            skLineSegment(sketch, "E77.MirrorCS", {"start": v(242.82, 59.26) * mm, "end": v(242.82, 63.5) * mm});
            skLineSegment(sketch, "E78.MirrorCS", {"start": v(157.1, 63.5) * mm, "end": v(157.1, 59.26) * mm});
            skArc(sketch, "E79.MirrorCS", {"start": v(192.4, 64.52) * mm, "mid": v(192.1, 63.8) * mm, "end": v(191.39, 63.5) * mm});
            skArc(sketch, "E80.MirrorCS", {"start": v(295.28, 64.52) * mm, "mid": v(294.98, 63.8) * mm, "end": v(294.26, 63.5) * mm});
            skLineSegment(sketch, "E81.MirrorCS", {"start": v(139.95, 63.5) * mm, "end": v(139.95, 59.26) * mm});
            skLineSegment(sketch, "E82.MirrorCS", {"start": v(122.8, 59.26) * mm, "end": v(122.8, 63.5) * mm});
            skArc(sketch, "E83.MirrorCS", {"start": v(175.26, 64.52) * mm, "mid": v(174.96, 63.8) * mm, "end": v(174.24, 63.5) * mm});
            skArc(sketch, "E84.MirrorCS", {"start": v(312.42, 64.52) * mm, "mid": v(312.12, 63.8) * mm, "end": v(311.4, 63.5) * mm});
            skArc(sketch, "E85.MirrorCS", {"start": v(55.25, 64.52) * mm, "mid": v(54.95, 63.8) * mm, "end": v(54.23, 63.5) * mm});
            skLineSegment(sketch, "E86.MirrorCS", {"start": v(277.11, 59.26) * mm, "end": v(277.11, 63.5) * mm});
            skLineSegment(sketch, "E87.MirrorCS", {"start": v(294.26, 63.5) * mm, "end": v(294.26, 59.26) * mm});
            skArc(sketch, "E88.MirrorCS", {"start": v(329.57, 64.52) * mm, "mid": v(329.27, 63.8) * mm, "end": v(328.55, 63.5) * mm});
            skArc(sketch, "E89.MirrorCS", {"start": v(158.12, 64.52) * mm, "mid": v(157.82, 63.8) * mm, "end": v(157.1, 63.5) * mm});
            skArc(sketch, "E90.MirrorCS", {"start": v(278.13, 64.52) * mm, "mid": v(277.83, 63.8) * mm, "end": v(277.11, 63.5) * mm});
            skArc(sketch, "E91.MirrorCS", {"start": v(123.83, 64.52) * mm, "mid": v(123.53, 63.8) * mm, "end": v(122.8, 63.5) * mm});
            skArc(sketch, "E92.MirrorCS", {"start": v(38.1, 64.52) * mm, "mid": v(37.8, 63.8) * mm, "end": v(37.08, 63.5) * mm});
            skArc(sketch, "E93.MirrorCS", {"start": v(209.55, 64.52) * mm, "mid": v(209.25, 63.8) * mm, "end": v(208.53, 63.5) * mm});
            skLineSegment(sketch, "E94.MirrorCS", {"start": v(38.1, 64.52) * mm, "end": v(38.1, 67.31) * mm});
            skArc(sketch, "E95.MirrorCS", {"start": v(89.54, 64.52) * mm, "mid": v(89.24, 63.8) * mm, "end": v(88.52, 63.5) * mm});
            skLineSegment(sketch, "E96.MirrorCS", {"start": v(54.23, 63.5) * mm, "end": v(54.23, 59.26) * mm});
            skArc(sketch, "E97.MirrorCS", {"start": v(363.86, 64.52) * mm, "mid": v(363.56, 63.8) * mm, "end": v(362.84, 63.5) * mm});
            skArc(sketch, "E98.MirrorCS", {"start": v(45.72, 63.5) * mm, "mid": v(45, 63.8) * mm, "end": v(44.7, 64.52) * mm});
            skLineSegment(sketch, "E99.MirrorCS", {"start": v(44.7, 66.5) * mm, "end": v(44.7, 64.52) * mm});
            skLineSegment(sketch, "E100.MirrorCS", {"start": v(336.17, 66.5) * mm, "end": v(336.17, 64.52) * mm});
            skLineSegment(sketch, "E101.MirrorCS", {"start": v(295.28, 64.52) * mm, "end": v(295.28, 67.31) * mm});
            skArc(sketch, "E102.MirrorCS", {"start": v(354.33, 63.5) * mm, "mid": v(353.61, 63.8) * mm, "end": v(353.31, 64.52) * mm});
            skArc(sketch, "E103.MirrorCS", {"start": v(234.31, 63.5) * mm, "mid": v(233.6, 63.8) * mm, "end": v(233.3, 64.52) * mm});
            skLineSegment(sketch, "E104.MirrorCS", {"start": v(175.26, 64.52) * mm, "end": v(175.26, 67.31) * mm});
            skLineSegment(sketch, "E105.MirrorCS", {"start": v(301.88, 66.5) * mm, "end": v(301.88, 64.52) * mm});
            skLineSegment(sketch, "E106.MirrorCS", {"start": v(147.57, 66.5) * mm, "end": v(147.57, 64.52) * mm});
            skArc(sketch, "E107.MirrorCS", {"start": v(268.6, 63.5) * mm, "mid": v(267.89, 63.8) * mm, "end": v(267.59, 64.52) * mm});
            skLineSegment(sketch, "E108.MirrorCS", {"start": v(209.55, 64.52) * mm, "end": v(209.55, 67.31) * mm});
            skArc(sketch, "E109.MirrorCS", {"start": v(80, 63.5) * mm, "mid": v(79.3, 63.8) * mm, "end": v(79, 64.52) * mm});
            skArc(sketch, "E110.MirrorCS", {"start": v(114.3, 63.5) * mm, "mid": v(113.58, 63.8) * mm, "end": v(113.28, 64.52) * mm});
            skLineSegment(sketch, "E111.MirrorCS", {"start": v(181.86, 66.5) * mm, "end": v(181.86, 64.52) * mm});
            skLineSegment(sketch, "E112.MirrorCS", {"start": v(267.59, 66.5) * mm, "end": v(267.59, 64.52) * mm});
            skLineSegment(sketch, "E113.MirrorCS", {"start": v(140.97, 64.52) * mm, "end": v(140.97, 67.31) * mm});
            skArc(sketch, "E114.MirrorCS", {"start": v(200.03, 63.5) * mm, "mid": v(199.3, 63.8) * mm, "end": v(199, 64.52) * mm});
            skLineSegment(sketch, "E115.MirrorCS", {"start": v(329.57, 64.52) * mm, "end": v(329.57, 67.31) * mm});
            skArc(sketch, "E116.MirrorCS", {"start": v(148.6, 63.5) * mm, "mid": v(147.87, 63.8) * mm, "end": v(147.57, 64.52) * mm});
            skLineSegment(sketch, "E117.MirrorCS", {"start": v(89.53, 64.52) * mm, "end": v(89.53, 67.31) * mm});
            skLineSegment(sketch, "E118.MirrorCS", {"start": v(216.15, 66.5) * mm, "end": v(216.15, 64.52) * mm});
            skLineSegment(sketch, "E119.MirrorCS", {"start": v(260.99, 64.52) * mm, "end": v(260.99, 67.31) * mm});
            skArc(sketch, "E120.MirrorCS", {"start": v(320.04, 63.5) * mm, "mid": v(319.32, 63.8) * mm, "end": v(319.02, 64.52) * mm});
            skLineSegment(sketch, "E121.MirrorCS", {"start": v(113.28, 66.5) * mm, "end": v(113.28, 64.52) * mm});
            skLineSegment(sketch, "E122.MirrorCS", {"start": v(363.86, 64.52) * mm, "end": v(363.86, 67.31) * mm});
            skLineSegment(sketch, "E123.MirrorCS", {"start": v(96.14, 66.5) * mm, "end": v(96.14, 64.52) * mm});
            skLineSegment(sketch, "E124.MirrorCS", {"start": v(243.84, 64.52) * mm, "end": v(243.84, 67.31) * mm});
            skLineSegment(sketch, "E125.MirrorCS", {"start": v(370.46, 66.5) * mm, "end": v(370.46, 64.52) * mm});
            skArc(sketch, "E126.MirrorCS", {"start": v(302.9, 63.5) * mm, "mid": v(302.18, 63.8) * mm, "end": v(301.88, 64.52) * mm});
            skLineSegment(sketch, "E127.MirrorCS", {"start": v(123.82, 64.52) * mm, "end": v(123.82, 67.31) * mm});
            skArc(sketch, "E128.MirrorCS", {"start": v(165.74, 63.5) * mm, "mid": v(165.02, 63.8) * mm, "end": v(164.72, 64.52) * mm});
            skLineSegment(sketch, "E129.MirrorCS", {"start": v(233.3, 66.5) * mm, "end": v(233.3, 64.52) * mm});
            skLineSegment(sketch, "E130.MirrorCS", {"start": v(106.68, 64.52) * mm, "end": v(106.68, 67.31) * mm});
            skLineSegment(sketch, "E131.MirrorCS", {"start": v(250.44, 66.5) * mm, "end": v(250.44, 64.52) * mm});
            skArc(sketch, "E132.MirrorCS", {"start": v(182.88, 63.5) * mm, "mid": v(182.16, 63.8) * mm, "end": v(181.86, 64.52) * mm});
            skLineSegment(sketch, "E133.MirrorCS", {"start": v(353.31, 66.5) * mm, "end": v(353.31, 64.52) * mm});
            skLineSegment(sketch, "E134.MirrorCS", {"start": v(226.7, 64.52) * mm, "end": v(226.7, 67.31) * mm});
            skArc(sketch, "E135.MirrorCS", {"start": v(285.75, 63.5) * mm, "mid": v(285.03, 63.8) * mm, "end": v(284.73, 64.52) * mm});
            skLineSegment(sketch, "E136.MirrorCS", {"start": v(79, 66.5) * mm, "end": v(79, 64.52) * mm});
            skLineSegment(sketch, "E137.MirrorCS", {"start": v(346.71, 64.52) * mm, "end": v(346.71, 67.31) * mm});
            skLineSegment(sketch, "E138.MirrorCS", {"start": v(199, 66.5) * mm, "end": v(199, 64.52) * mm});
            skLineSegment(sketch, "E139.MirrorCS", {"start": v(72.4, 64.52) * mm, "end": v(72.4, 67.31) * mm});
            skArc(sketch, "E140.MirrorCS", {"start": v(131.44, 63.5) * mm, "mid": v(130.73, 63.8) * mm, "end": v(130.43, 64.52) * mm});
            skLineSegment(sketch, "E141.MirrorCS", {"start": v(319.02, 66.5) * mm, "end": v(319.02, 64.52) * mm});
            skLineSegment(sketch, "E142.MirrorCS", {"start": v(164.72, 66.5) * mm, "end": v(164.72, 64.52) * mm});
            skArc(sketch, "E143.MirrorCS", {"start": v(97.15, 63.5) * mm, "mid": v(96.44, 63.8) * mm, "end": v(96.14, 64.52) * mm});
            skLineSegment(sketch, "E144.MirrorCS", {"start": v(37.08, 63.5) * mm, "end": v(37.08, 59.26) * mm});
            skLineSegment(sketch, "E145.MirrorCS", {"start": v(130.43, 66.5) * mm, "end": v(130.43, 64.52) * mm});
            skArc(sketch, "E146.MirrorCS", {"start": v(251.46, 63.5) * mm, "mid": v(250.74, 63.8) * mm, "end": v(250.44, 64.52) * mm});
            skLineSegment(sketch, "E147.MirrorCS", {"start": v(192.4, 64.52) * mm, "end": v(192.4, 67.31) * mm});
            skArc(sketch, "E148.MirrorCS", {"start": v(62.87, 63.5) * mm, "mid": v(62.15, 63.8) * mm, "end": v(61.85, 64.52) * mm});
            skLineSegment(sketch, "E149.MirrorCS", {"start": v(278.13, 64.52) * mm, "end": v(278.13, 67.31) * mm});
            skLineSegment(sketch, "E150.MirrorCS", {"start": v(61.85, 66.5) * mm, "end": v(61.85, 64.52) * mm});
            skArc(sketch, "E151.MirrorCS", {"start": v(337.19, 63.5) * mm, "mid": v(336.47, 63.8) * mm, "end": v(336.17, 64.52) * mm});
            skLineSegment(sketch, "E152.MirrorCS", {"start": v(158.12, 64.52) * mm, "end": v(158.12, 67.31) * mm});
            skLineSegment(sketch, "E153.MirrorCS", {"start": v(284.73, 66.5) * mm, "end": v(284.73, 64.52) * mm});
            skArc(sketch, "E154.MirrorCS", {"start": v(217.17, 63.5) * mm, "mid": v(216.45, 63.8) * mm, "end": v(216.15, 64.52) * mm});
            skArc(sketch, "E155.MirrorCS", {"start": v(371.48, 63.5) * mm, "mid": v(370.76, 63.8) * mm, "end": v(370.46, 64.52) * mm});
            skLineSegment(sketch, "E156.MirrorCS", {"start": v(312.42, 64.52) * mm, "end": v(312.42, 67.31) * mm});
            skPoint(sketch, "E157.MirrorP", {"position": v(226.7, 63.5) * mm});
            skLineSegment(sketch, "E158.MirrorCS", {"start": v(38.1, 67.31) * mm, "end": v(55.25, 67.31) * mm, "construction": true});
            skPoint(sketch, "E159.MirrorP", {"position": v(295.28, 63.5) * mm});
            skArc(sketch, "E160.MirrorCS", {"start": v(38.1, 67.31) * mm, "mid": v(41.76, 69.82) * mm, "end": v(44.7, 66.5) * mm});
            skPoint(sketch, "E161.MirrorP", {"position": v(38.1, 63.5) * mm});
            skPoint(sketch, "E162.MirrorP", {"position": v(44.7, 63.5) * mm});
            skLineSegment(sketch, "E163.MirrorCS", {"start": v(302.9, 63.5) * mm, "end": v(311.4, 63.5) * mm});
            skArc(sketch, "E164.MirrorCS", {"start": v(260.99, 67.31) * mm, "mid": v(264.65, 69.82) * mm, "end": v(267.59, 66.5) * mm});
            skLineSegment(sketch, "E165.MirrorCS", {"start": v(311.4, 59.26) * mm, "end": v(328.55, 59.26) * mm});
            skPoint(sketch, "E166.MirrorP", {"position": v(55.25, 63.5) * mm});
            skPoint(sketch, "E167.MirrorP", {"position": v(284.73, 63.5) * mm});
            skLineSegment(sketch, "E168.MirrorCS", {"start": v(191.39, 59.26) * mm, "end": v(208.53, 59.26) * mm});
            skPoint(sketch, "E169.MirrorP", {"position": v(329.57, 63.5) * mm});
            skArc(sketch, "E170.MirrorCS", {"start": v(140.97, 67.31) * mm, "mid": v(144.63, 69.82) * mm, "end": v(147.57, 66.5) * mm});
            skLineSegment(sketch, "E171.MirrorCS", {"start": v(268.6, 63.5) * mm, "end": v(277.11, 63.5) * mm});
            skLineSegment(sketch, "E172.MirrorCS", {"start": v(225.68, 59.26) * mm, "end": v(242.82, 59.26) * mm});
            skPoint(sketch, "E173.MirrorP", {"position": v(336.17, 63.5) * mm});
            skLineSegment(sketch, "E174.MirrorCS", {"start": v(114.3, 63.5) * mm, "end": v(122.8, 63.5) * mm});
            skPoint(sketch, "E175.MirrorP", {"position": v(61.85, 63.5) * mm});
            skArc(sketch, "E176.MirrorCS", {"start": v(175.26, 67.31) * mm, "mid": v(178.92, 69.82) * mm, "end": v(181.86, 66.5) * mm});
            skPoint(sketch, "E177.MirrorP", {"position": v(106.68, 63.5) * mm});
            skPoint(sketch, "E178.MirrorP", {"position": v(278.13, 63.5) * mm});
            skPoint(sketch, "E179.MirrorP", {"position": v(233.3, 63.5) * mm});
            skLineSegment(sketch, "E180.MirrorCS", {"start": v(71.37, 59.26) * mm, "end": v(88.52, 59.26) * mm});
            skLineSegment(sketch, "E181.MirrorCS", {"start": v(157.1, 59.26) * mm, "end": v(174.24, 59.26) * mm});
            skLineSegment(sketch, "E182.MirrorCS", {"start": v(148.6, 63.5) * mm, "end": v(157.1, 63.5) * mm});
            skLineSegment(sketch, "E183.MirrorCS", {"start": v(345.7, 59.26) * mm, "end": v(362.84, 59.26) * mm});
            skLineSegment(sketch, "E184.MirrorCS", {"start": v(234.31, 63.5) * mm, "end": v(242.82, 63.5) * mm});
            skArc(sketch, "E185.MirrorCS", {"start": v(295.27, 67.31) * mm, "mid": v(298.94, 69.82) * mm, "end": v(301.88, 66.5) * mm});
            skArc(sketch, "E186.MirrorCS", {"start": v(106.68, 67.31) * mm, "mid": v(110.34, 69.82) * mm, "end": v(113.28, 66.5) * mm});
            skPoint(sketch, "E187.MirrorP", {"position": v(113.28, 63.5) * mm});
            skPoint(sketch, "E188.MirrorP", {"position": v(158.12, 63.5) * mm});
            skPoint(sketch, "E189.MirrorP", {"position": v(175.26, 63.5) * mm});
            skPoint(sketch, "E190.MirrorP", {"position": v(130.43, 63.5) * mm});
            skLineSegment(sketch, "E191.MirrorCS", {"start": v(105.66, 59.26) * mm, "end": v(122.8, 59.26) * mm});
            skLineSegment(sketch, "E192.MirrorCS", {"start": v(182.88, 63.5) * mm, "end": v(191.39, 63.5) * mm});
            skLineSegment(sketch, "E193.MirrorCS", {"start": v(277.11, 59.26) * mm, "end": v(294.26, 59.26) * mm});
            skLineSegment(sketch, "E194.MirrorCS", {"start": v(354.33, 63.5) * mm, "end": v(362.84, 63.5) * mm});
            skLineSegment(sketch, "E195.MirrorCS", {"start": v(80, 63.5) * mm, "end": v(88.52, 63.5) * mm});
            skArc(sketch, "E196.MirrorCS", {"start": v(226.7, 67.31) * mm, "mid": v(230.36, 69.82) * mm, "end": v(233.3, 66.5) * mm});
            skPoint(sketch, "E197.MirrorP", {"position": v(209.55, 63.5) * mm});
            skArc(sketch, "E198.MirrorCS", {"start": v(329.56, 67.31) * mm, "mid": v(333.23, 69.82) * mm, "end": v(336.17, 66.5) * mm});
            skPoint(sketch, "E199.MirrorP", {"position": v(164.72, 63.5) * mm});
            skPoint(sketch, "E200.MirrorP", {"position": v(79, 63.5) * mm});
            skPoint(sketch, "E201.MirrorP", {"position": v(123.82, 63.5) * mm});
            skPoint(sketch, "E202.MirrorP", {"position": v(353.31, 63.5) * mm});
            skLineSegment(sketch, "E203.MirrorCS", {"start": v(259.97, 59.26) * mm, "end": v(277.11, 59.26) * mm});
            skArc(sketch, "E204.MirrorCS", {"start": v(209.55, 67.31) * mm, "mid": v(213.21, 69.82) * mm, "end": v(216.15, 66.5) * mm});
            skLineSegment(sketch, "E205.MirrorCS", {"start": v(337.19, 63.5) * mm, "end": v(345.7, 63.5) * mm});
            skPoint(sketch, "E206.MirrorP", {"position": v(72.4, 63.5) * mm});
            skArc(sketch, "E207.MirrorCS", {"start": v(346.7, 67.31) * mm, "mid": v(350.37, 69.82) * mm, "end": v(353.31, 66.5) * mm});
            skLineSegment(sketch, "E208.MirrorCS", {"start": v(122.8, 59.26) * mm, "end": v(139.95, 59.26) * mm});
            skPoint(sketch, "E209.MirrorP", {"position": v(346.71, 63.5) * mm});
            skLineSegment(sketch, "E210.MirrorCS", {"start": v(139.95, 59.26) * mm, "end": v(157.1, 59.26) * mm});
            skPoint(sketch, "E211.MirrorP", {"position": v(301.88, 63.5) * mm});
            skLineSegment(sketch, "E212.MirrorCS", {"start": v(200.03, 63.5) * mm, "end": v(208.53, 63.5) * mm});
            skArc(sketch, "E213.MirrorCS", {"start": v(89.53, 67.31) * mm, "mid": v(93.2, 69.82) * mm, "end": v(96.14, 66.5) * mm});
            skArc(sketch, "E214.MirrorCS", {"start": v(72.4, 67.31) * mm, "mid": v(76.05, 69.82) * mm, "end": v(79, 66.5) * mm});
            skPoint(sketch, "E215.MirrorP", {"position": v(216.15, 63.5) * mm});
            skPoint(sketch, "E216.MirrorP", {"position": v(260.99, 63.5) * mm});
            skLineSegment(sketch, "E217.MirrorCS", {"start": v(217.17, 63.5) * mm, "end": v(225.68, 63.5) * mm});
            skArc(sketch, "E218.MirrorCS", {"start": v(363.86, 67.31) * mm, "mid": v(367.52, 69.82) * mm, "end": v(370.46, 66.5) * mm});
            skLineSegment(sketch, "E219.MirrorCS", {"start": v(320.04, 63.5) * mm, "end": v(328.55, 63.5) * mm});
            skArc(sketch, "E220.MirrorCS", {"start": v(192.4, 67.31) * mm, "mid": v(196.07, 69.82) * mm, "end": v(199, 66.5) * mm});
            skLineSegment(sketch, "E221.MirrorCS", {"start": v(242.82, 59.26) * mm, "end": v(259.97, 59.26) * mm});
            skPoint(sketch, "E222.MirrorP", {"position": v(267.59, 63.5) * mm});
            skPoint(sketch, "E223.MirrorP", {"position": v(312.42, 63.5) * mm});
            skArc(sketch, "E224.MirrorCS", {"start": v(312.42, 67.31) * mm, "mid": v(316.08, 69.82) * mm, "end": v(319.02, 66.5) * mm});
            skLineSegment(sketch, "E225.MirrorCS", {"start": v(362.84, 59.26) * mm, "end": v(374.4, 59.26) * mm});
            skPoint(sketch, "E226.MirrorP", {"position": v(147.57, 63.5) * mm});
            skLineSegment(sketch, "E227.MirrorCS", {"start": v(54.23, 59.26) * mm, "end": v(71.37, 59.26) * mm});
            skPoint(sketch, "E228.MirrorP", {"position": v(192.4, 63.5) * mm});
            skLineSegment(sketch, "E229.MirrorCS", {"start": v(88.52, 59.26) * mm, "end": v(105.66, 59.26) * mm});
            skPoint(sketch, "E230.MirrorP", {"position": v(319.02, 63.5) * mm});
            skLineSegment(sketch, "E231.MirrorCS", {"start": v(165.74, 63.5) * mm, "end": v(174.24, 63.5) * mm});
            skPoint(sketch, "E232.MirrorP", {"position": v(363.86, 63.5) * mm});
            skLineSegment(sketch, "E233.MirrorCS", {"start": v(131.44, 63.5) * mm, "end": v(139.95, 63.5) * mm});
            skPoint(sketch, "E234.MirrorP", {"position": v(140.97, 63.5) * mm});
            skLineSegment(sketch, "E235.MirrorCS", {"start": v(37.08, 59.26) * mm, "end": v(54.23, 59.26) * mm});
            skPoint(sketch, "E236.MirrorP", {"position": v(96.14, 63.5) * mm});
            skArc(sketch, "E237.MirrorCS", {"start": v(158.12, 67.31) * mm, "mid": v(161.78, 69.82) * mm, "end": v(164.72, 66.5) * mm});
            skPoint(sketch, "E238.MirrorP", {"position": v(370.46, 63.5) * mm});
            skLineSegment(sketch, "E239.MirrorCS", {"start": v(285.75, 63.5) * mm, "end": v(294.26, 63.5) * mm});
            skLineSegment(sketch, "E240.MirrorCS", {"start": v(208.53, 59.26) * mm, "end": v(225.68, 59.26) * mm});
            skPoint(sketch, "E241.MirrorP", {"position": v(250.44, 63.5) * mm});
            skLineSegment(sketch, "E242.MirrorCS", {"start": v(97.15, 63.5) * mm, "end": v(105.66, 63.5) * mm});
            skArc(sketch, "E243.MirrorCS", {"start": v(243.84, 67.31) * mm, "mid": v(247.5, 69.82) * mm, "end": v(250.44, 66.5) * mm});
            skLineSegment(sketch, "E244.MirrorCS", {"start": v(371.48, 63.5) * mm, "end": v(374.4, 63.5) * mm});
            skArc(sketch, "E245.MirrorCS", {"start": v(55.25, 67.31) * mm, "mid": v(58.9, 69.82) * mm, "end": v(61.85, 66.5) * mm});
            skLineSegment(sketch, "E246.MirrorCS", {"start": v(294.26, 59.26) * mm, "end": v(311.4, 59.26) * mm});
            skLineSegment(sketch, "E247.MirrorCS", {"start": v(62.87, 63.5) * mm, "end": v(71.37, 63.5) * mm});
            skLineSegment(sketch, "E248.MirrorCS", {"start": v(45.72, 63.5) * mm, "end": v(54.23, 63.5) * mm});
            skPoint(sketch, "E249.MirrorP", {"position": v(89.53, 63.5) * mm});
            skArc(sketch, "E250.MirrorCS", {"start": v(123.82, 67.31) * mm, "mid": v(127.49, 69.82) * mm, "end": v(130.43, 66.5) * mm});
            skPoint(sketch, "E251.MirrorP", {"position": v(243.84, 63.5) * mm});
            skPoint(sketch, "E252.MirrorP", {"position": v(199, 63.5) * mm});
            skLineSegment(sketch, "E253.MirrorCS", {"start": v(251.46, 63.5) * mm, "end": v(259.97, 63.5) * mm});
            skLineSegment(sketch, "E254.MirrorCS", {"start": v(174.24, 59.26) * mm, "end": v(191.39, 59.26) * mm});
            skPoint(sketch, "E255.MirrorP", {"position": v(181.86, 63.5) * mm});
            skArc(sketch, "E256.MirrorCS", {"start": v(278.13, 67.31) * mm, "mid": v(281.8, 69.82) * mm, "end": v(284.73, 66.5) * mm});
            skLineSegment(sketch, "E257.MirrorCS", {"start": v(328.55, 59.26) * mm, "end": v(345.7, 59.26) * mm});
            skLineSegment(sketch, "E258", {"start": v(374.4, 12.7) * mm, "end": v(374.4, 16.94) * mm});
            skPoint(sketch, "E37.19.0.8.start.orphan", {"position": v(379.98, 16.94) * mm});
            skPoint(sketch, "E259.orphan", {"position": v(379.98, 12.7) * mm});
            skLineSegment(sketch, "E260", {"start": v(374.4, 63.5) * mm, "end": v(374.4, 59.26) * mm});
            skPoint(sketch, "E261.MirrorCS.end.orphan", {"position": v(379.98, 63.5) * mm});
            skPoint(sketch, "E261.MirrorCS.start.orphan", {"position": v(379.98, 59.26) * mm});
            skSolve(sketch);
        }
        {
            var Q0;
            Q0 = qSketchRegion(id + "F7", true);
            extrude(context, id + "F8", {"entities" : qUnion([Q0]), "operationType" : NewBodyOperationType.REMOVE, "oppositeDirection" : true, "depth" : 25.4 * mm});
        }
        {
            var Q0;
            Q0=qCreatedBy(makeId("Top.planeOp"),FACE);
            var sketch = newSketch(context, id + "F9", { "sketchPlane" : qUnion([Q0])});
            skLineSegment(sketch, "E262.bottom", {"start": v(34, -104.57) * mm, "end": v(40.35, -104.57) * mm});
            skLineSegment(sketch, "E262.top", {"start": v(34, -47.42) * mm, "end": v(40.35, -47.42) * mm});
            skLineSegment(sketch, "E262.left", {"start": v(34, -104.57) * mm, "end": v(34, -47.42) * mm});
            skLineSegment(sketch, "E262.right", {"start": v(40.35, -104.57) * mm, "end": v(40.35, -47.42) * mm});
            skSolve(sketch);
        }
        {
            var Q0;
            Q0 = qSketchRegion(id + "F9", true);
            extrude(context, id + "F10", {"entities" : qUnion([Q0]), "depth" : 114.3 * mm});
        }
        {
            var Q0;
            Q0=makeQuery(id+"F10.opExtrude","SWEPT_FACE",FACE,{"disambiguationData":[OSD([sQuery(id+"F9.wireOp",EDGE,"E262.right")])]});
            var sketch = newSketch(context, id + "F11", { "sketchPlane" : qUnion([Q0])});
            skLineSegment(sketch, "E263.bottom", {"start": v(-114.1, 107.95) * mm, "end": v(-37.9, 107.95) * mm});
            skLineSegment(sketch, "E263.top", {"start": v(-114.1, 120.65) * mm, "end": v(-37.9, 120.65) * mm});
            skLineSegment(sketch, "E263.left", {"start": v(-114.1, 107.95) * mm, "end": v(-114.1, 120.65) * mm});
            skLineSegment(sketch, "E263.right", {"start": v(-37.9, 107.95) * mm, "end": v(-37.9, 120.65) * mm});
            skPoint(sketch, "E263.middle", {"position": v(-76, 114.3) * mm});
            skSolve(sketch);
        }
        {
            var Q0;
            Q0 = qSketchRegion(id + "F11", true);
            extrude(context, id + "F12", {"entities" : qUnion([Q0]), "operationType" : NewBodyOperationType.ADD, "oppositeDirection" : true, "depth" : 6.35 * mm});
        }
        {
            var Q0;
            Q0=makeQuery(id+"F12.opExtrude","SWEPT_EDGE",EDGE,{"disambiguationData":[OSD([sQuery(id+"F11.wireOp",EDGE,"E263.top"),sQuery(id+"F11.wireOp",EDGE,"E263.right")])]});
            var Q1;
            Q1=makeQuery(id+"F12.opExtrude","SWEPT_EDGE",EDGE,{"disambiguationData":[OSD([sQuery(id+"F11.wireOp",EDGE,"E263.top"),sQuery(id+"F11.wireOp",EDGE,"E263.left")])]});
            fillet(context, id + "F13", {"entities" : qUnion([Q0, Q1]), "radius" : 6.35 * mm, "tangentPropagation" : true, "allowEdgeOverflow" : false});
        }
    });
